# Revit family: IS_iLifeB_T5091_BIM_NL
name_source: partatom
category: Plumbing Fixtures
units: mm (PartAtom-declared; Revit-internal decimal feet)

## family parameters
Always vertical = No
Cut with Voids When Loaded = No
OmniClass Number = 23.45.05.14.14
OmniClass Title = Sinks/Lavatories
Part Type = Normal
Room Calculation Point = No
Round Connector Dimension = Use Diameter
Shared = No
Work Plane-Based = No

## types (2) — shared parameters
Afmetingen = 400 x 400 x 142 mm
AfstandsEenheid = Millimeter
Auteur = Ideal Standard
BIMobject category = Wash basins
BIMobject category code = wash-basins
BIMobject main category = Sanitary
BIMobject main category code = sanitary
Beschrijvinggarantie = Herstellergarantie
Bestanddelen = https://www.idealstandard.nl
BimObjectNaam = IS_IdealStandard_Vesselbasins_iLifeB_T5091
Brand url = https://www.idealstandard.nl
Date of publishing = 24/02/2023
Diepte = 400 mm
DuurEenheid = Jahr
Edition number = 1
Garantieunits = Jahre
GemaaktOp = 24/2/2023
Hoogte = 141,509490966797
IFC Classification = Sanitary Terminal
IfcExportAs = IfcSanitaryTerminalType
IfcExportType = WASHHANDBASIN
Installatieinstructies = https://www.idealstandard.nl
Installation instructions = https://www.idealstandard.nl
Lengte = 400 mm
Manufacturer = Ideal Standard
Manufacturer name = Ideal Standard
Materiaal = Keramik
Material main = Ceramics
Merk = Ideal Standard
NBS Reference Code = 35-65-70-94
NBS Reference Description = Wash Basin Systems
Nettogewicht = 8.5
NominalDepth = 400 mm
NominalHeight = 142 mm
NominalWidth = 401 mm
OmniClass Code = 23-31 13 00
OmniClass Description = Sinks
OppervlakteAfmeting = Millimeter
OppervlakteEenheid = Millimeter
Product Guid = cac0b904-5831-4666-897c-9fd879467323
Product SKU = T5091
Product certification = https://www.idealstandard.nl
Product data url = https://bimobject.com
Product family = Ideal Standard i.life B
Product group = Ideal Standard i.life B
Product name = I.LIFE B VESSEL ROUND 40 OF WHT BXD
Product url = https://www.idealstandard.nl
ProductSoort = WASTAFEL
Productinformatie = https://www.idealstandard.nl
QR code = http://bimobject.com
Revisie = 1
Size = 400 x 400 x 142 mm
Technical description = https://www.idealstandard.nl
Telefoonnummer = 077 355 08 08
Typeconnectie = Installation
Typewastafel = Schale
UNSPSC Code = 301815
URL = https://www.idealstandard.nl
Uniclass 2015 Code = Pr_40_20_96
Uniclass 2015 Name = Wash basins, sinks and troughs
Uniclass2015Beschrijving = Wash basins, sinks and troughs
Uniclass2015Referentie = Wash basins, sinks and troughs
Uniclass2015Version = Products v1.22
Uniformat II Code = D2010
Uniformat II Description = Plumbing Fixtures
Urlproducent = https://www.idealstandard.nl
ValutaEenheid = €
Versie = 1
Volumeunits = Liter
Vorm = Skulptur
Wisselstukken = https://www.idealstandard.nl
Youtube clip = https://www.youtube.com
zero-valued in all types: BrutoGewicht, Cost, Default Elevation, Vervangingskosten

## per-type parameters (varying)
| type | Afwerking | Artikelnummer | Artikelomschrijving | Barcode | Breedte | Description | GTIN code | Kleur | Model |
| T509101 - Ideal Standard i.life B vessel round Ø40cm with overflow, white, in carton box, EU pallet | Wit | T509101 | Schale rund Ø40cm mit Überlauf, weiß, im Karton, EU-Palette | 8014140509844 | 600.1218 | Ideal Standard i.life B vessel round Ø40cm with overflow, white, in carton box, EU pallet | 8014140509844 | Wit | T509101 |
| T5091MA - Ideal Standard i.life B vessel round Ø40cm with overflow, white, Ideal Plus, in carton box, EU pallet | Wit Ideal Plus | T5091MA | Schale rund Ø40cm mit Überlauf, weiß, Ideal Plus, im Karton, EU-Palette | 8014140515388 | 400.592636 | Ideal Standard i.life B vessel round Ø40cm with overflow, white, Ideal Plus, in carton box, EU pallet | 8014140515388 | Wit Ideal Plus | T5091MA |

## geometry (parser evidence)
native form markers: Blend x4, Sweep x3
no freeform markers — native parametric forms only
